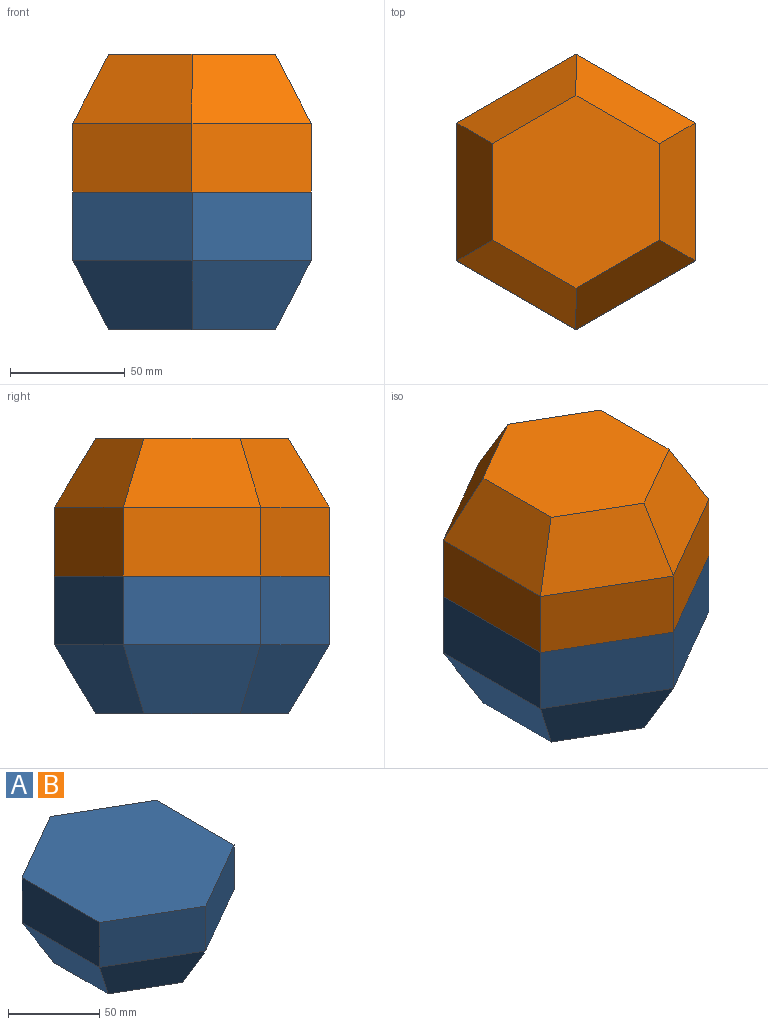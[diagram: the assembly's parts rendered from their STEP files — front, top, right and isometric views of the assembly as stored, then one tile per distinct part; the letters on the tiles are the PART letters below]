
ASSEMBLY  parts=2 mates=1
PART A: 14 faces, bbox 103.9x120x60 mm
  f0: plane 84x72.75mm, normal (0,0,-1), area 4583mm2, adj f1,f2,f3,f4,f5,f6
  f1: plane 51.96x39mm, normal (0.44,-0.77,-0.46), area 1724.2mm2, adj f0,f2,f6,f7
  f2: plane 60x30mm, normal (0.89,0,-0.46), area 1724.2mm2, adj f0,f1,f3,f8
  f3: plane 51.96x39mm, normal (0.44,0.77,-0.46), area 1724.2mm2, adj f0,f2,f4,f9
  f4: plane 51.96x39mm, normal (-0.44,0.77,-0.46), area 1724.2mm2, adj f0,f3,f5,f10
  f5: plane 60x30mm, normal (-0.89,0,-0.46), area 1724.2mm2, adj f0,f4,f6,f11
  f6: plane 51.96x39mm, normal (-0.44,-0.77,-0.46), area 1724.2mm2, adj f0,f1,f5,f12
  f7: plane 51.96x30mm, normal (0.5,-0.87,0), area 1800mm2, adj f1,f8,f12,f13
  f8: plane 60x30mm, normal (1,0,0), area 1800mm2, adj f2,f7,f9,f13
  f9: plane 51.96x30mm, normal (0.5,0.87,0), area 1800mm2, adj f3,f8,f10,f13
  f10: plane 51.96x30mm, normal (-0.5,0.87,0), area 1800mm2, adj f4,f9,f11,f13
  f11: plane 60x30mm, normal (-1,0,0), area 1800mm2, adj f5,f10,f12,f13
  f12: plane 51.96x30mm, normal (-0.5,-0.87,0), area 1800mm2, adj f6,f7,f11,f13
  f13: plane 120x103.92mm, normal (0,0,1), area 9353.1mm2, adj f7,f8,f9,f10,f11,f12
PART B: same geometry as A
PLACE A t=(0,0,11.1)mm
PLACE B rot(axis=(0,1,0),180deg) t=(0,0,131.1)mm
MATE fastened A.f13 <-> B.f13  axis (0,0,1) through (0,0,71.1)mm
